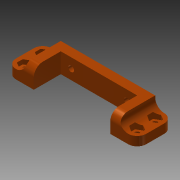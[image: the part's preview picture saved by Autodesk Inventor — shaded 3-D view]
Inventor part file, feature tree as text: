
AUTODESK INVENTOR PART (.ipt)
format: ipt  version: 2013 (Build 170138000, 138)  size: 199,680 bytes
history: native  units: mm
features: extrude x5, sketch x5, projected_geometry x2, fillet x1
ambient origin geometry x8: Origin, YZ Plane, XZ Plane, XY Plane, X Axis, Y Axis, Z Axis, Center Point
bodies: Solid1 (feature_tree)
feature tree (13):
  extrude  "Extrusion1"  Depth=20.0mm
  extrude  "Extrusion2"  Depth=5.0mm
  extrude  "Extrusion3"  Depth=5.0mm
  extrude  "Extrusion4"  Depth=6.0mm TaperAngle=0.0deg
  fillet  "Fillet1"  Radius=10.0mm
  extrude  "Extrusion5"  Depth=5.0mm TaperAngle=0.0deg
  sketch  "Sketch1"  dims[d0=42.5mm d2=20.0mm]
  sketch  "Sketch2"  dims[d3=15.0mm d4=5.0mm]
  sketch  "Sketch3"  dims[d5=5.0mm d6=0.0mm d7=5.0mm]
  projected_geometry  "Projected Loop1"
  sketch  "Sketch4"  dims[d8=5.0mm d9=6.0mm d10=0.0mm d11=10.0mm]
  projected_geometry  "Projected Loop2"
  sketch  "Sketch5"  dims[d13=3.2mm d14=5.0mm d15=0.0mm d16=5.6mm d17=2.5mm d18=0.0mm d19=5.0mm d20=42.0mm d22=31.0mm d23=3.2mm d24=2.5mm d25=0.0mm]
